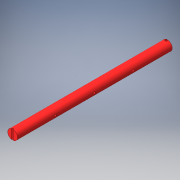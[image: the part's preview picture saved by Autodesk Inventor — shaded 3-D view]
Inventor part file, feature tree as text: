
AUTODESK INVENTOR PART (.ipt)
format: ipt  version: 2016 (Build 200138000, 138)  size: 135,680 bytes
history: native  units: in
note: dims shown in document units (in); Inventor stores cm internally (conversion verified against a paired STEP export)
features: extrude x4, sketch x3
ambient origin geometry x8: Origin, YZ Plane, XZ Plane, XY Plane, X Axis, Y Axis, Z Axis, Center Point
bodies: Solid1 (feature_tree)
feature tree (7):
  extrude  "Extrusion1"  Depth=8.0in TaperAngle=0.0deg
  extrude  "Extrusion4"  Depth=0.06in
  extrude  "Extrusion8"  Depth=2.0in TaperAngle=0.0deg
  extrude  "Extrusion9"  Depth=2.0in
  sketch  "Sketch1"  dims[d0=0.5in d1=8.0in d2=0.0in]
  sketch  "Sketch4"  dims[d13=0.06in d15=0.06in]
  sketch  "Sketch7"  dims[d16=0.1in d17=0.6in d18=0.0in d19=0.1in d20=0.06in d21=0.05in d26=0.5in d27=0.06in d42=2.0in d43=0.1in d44=2.0in d45=0.1in d46=2.0in d47=0.1in d48=1.0in d49=0.0in d50=1.0in d51=0.0in]
